# Revit family: STH8745_30_STH8746_30
name_source: partatom
category: Luminárias
units: mm (PartAtom-declared; Revit-internal decimal feet)

## family parameters
Com base no plano de trabalho = Não
Compartilhado = Não
Corte com vazios quando carregada = Não
Cota do conector redondo = Utilizar diâmetro
Fonte luminosa = Sim
Manter orientação da anotação = Não
Ponto de cálculo do ambiente = Não
Sempre na vertical = Sim
Tipo de parte = Normal

## types (2) — shared parameters
Altura = 0.05 m
Arquivo de rede fotométrica = STELLA - STH8745-30 - MINI NEU 2.ies
Comprimento = 0.07 m
Dimerização = Não dimerizável
Fabricante = Stella
Filtro de cor = 16777215
Fluxo Luminoso = 40 lm
Grau de proteção (IP) = IP65
Largura = 0.01 m
Luminoso = Luminoso - 3000K
Modelo = Mini Neu 2
Potência = 2 W
Temperatura da cor (K) = 3000 K
Tensão Elétrica = 100V-240V
Troca de temperatura da cor de lâmpada com esmaecimento = <Nenhum>
URL = https://stella.com.br
Ângulo de Abertura = 60°
Ângulo de inclinação = 90.00°
zero-valued in all types: Elevação padrão

## per-type parameters (varying)
| type | Estrutura | Referência |
| STH8745/30 - BRANCO - BIVOLT - 3000K - 40lm | Al - Branco | STH8745/30 - BIVOLT |
| STH8746/30 - PRETO - BIVOLT - 3000K - 40lm | Al - Preto | STH8746/30 - BIVOLT |
